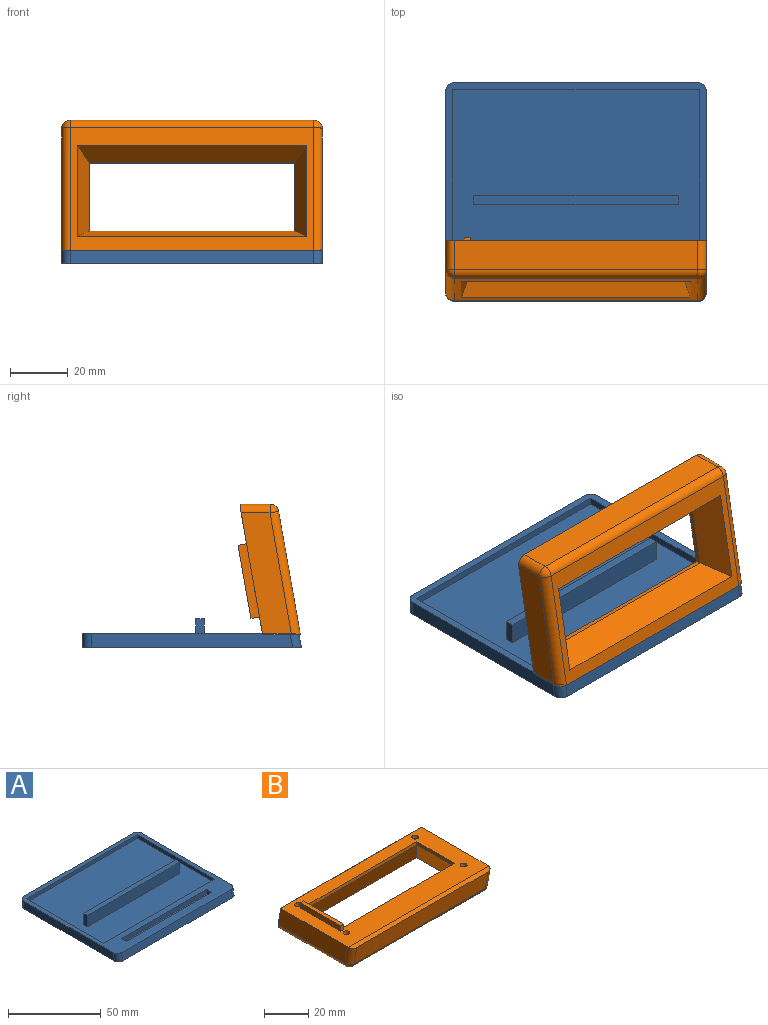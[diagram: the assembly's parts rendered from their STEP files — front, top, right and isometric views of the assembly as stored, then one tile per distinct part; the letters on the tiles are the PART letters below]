
ASSEMBLY  parts=2 mates=1
PART A: 25 faces, bbox 90x75.5x10.5 mm
  f0: plane 85x59.56mm, normal (0,0,1), area 4851mm2, adj f1,f2,f3,f4,f21,f22,f23,f24
  f1: plane 59.56x2.5mm, normal (-1,0,0), area 148.3mm2, adj f0,f2,f3,f9
  f2: plane 85x2.5mm, normal (0,-1,0), area 212.5mm2, adj f0,f1,f4,f9
  f3: plane 85x2.5mm, normal (0,0.98,-0.17), area 215.8mm2, adj f0,f1,f4,f9
  f4: plane 59.56x2.5mm, normal (1,0,0), area 148.3mm2, adj f0,f2,f3,f9
  f5: cylinder r=3mm len=5mm, axis (0,0,1), area 23.6mm2, adj f6,f8,f9,f11
  f6: plane 84x5mm, normal (0,1,0), area 420mm2, adj f5,f7,f8,f9
  f7: cylinder r=3mm len=5mm, axis (0,0,-1), area 23.6mm2, adj f6,f8,f9,f12
  f8: plane 90x75.5mm, normal (0,0,-1), area 6787.2mm2, adj f5,f6,f7,f10,f11,f12,f18,f19
  f9: plane 90x74.62mm, normal (0,0,1), area 1421.9mm2, adj f1,f2,f3,f4,f5,f6,f7,f10
  f10: plane 84x5mm, normal (0,-0.98,0.17), area 426.5mm2, adj f8,f9,f18,f19
  f11: plane 69.45x5mm, normal (-1,0,0), area 345.1mm2, adj f5,f8,f9,f18
  f12: plane 69.45x5mm, normal (1,0,0), area 345.1mm2, adj f7,f8,f9,f19
  f13: plane 65.22x3mm, normal (0,-1,0), area 195.7mm2, adj f9,f14,f16,f17
  f14: plane 4x3mm, normal (1,0,0), area 12mm2, adj f9,f13,f15,f17
  f15: plane 65.22x3mm, normal (0,1,0), area 195.7mm2, adj f9,f14,f16,f17
  f16: plane 4x3mm, normal (-1,0,0), area 12mm2, adj f9,f13,f15,f17
  f17: plane 65.22x4mm, normal (0,0,1), area 260.9mm2, adj f13,f14,f15,f16
  f18: cylinder r=3mm len=6.04mm, axis (0,0.17,0.98), area 23.9mm2, adj f8,f9,f10,f11
  f19: cylinder r=3mm len=6.04mm, axis (0,-0.17,-0.98), area 23.9mm2, adj f8,f9,f10,f12
  f20: plane 70.5x3mm, normal (0,0,1), area 211.5mm2, adj f21,f22,f23,f24
  f21: plane 7.5x3mm, normal (1,0,0), area 22.5mm2, adj f0,f20,f22,f24
  f22: plane 70.5x7.5mm, normal (0,-1,0), area 528.7mm2, adj f0,f20,f21,f23
  f23: plane 7.5x3mm, normal (-1,0,0), area 22.5mm2, adj f0,f20,f22,f24
  f24: plane 70.5x7.5mm, normal (0,1,0), area 528.7mm2, adj f0,f20,f21,f23
PART B: 40 faces, bbox 90x49.2x15.8 mm
  f0: plane 2.37x2.37mm, normal (0,0,1), area 4.4mm2, adj f12
  f1: plane 2.37x2.37mm, normal (0,0,1), area 4.4mm2, adj f13
  f2: plane 2.37x2.37mm, normal (0,0,1), area 4.4mm2, adj f14
  f3: plane 2.37x2.37mm, normal (0,0,1), area 4.4mm2, adj f15
  f4: plane 84x9.89mm, normal (0,-0.98,-0.17), area 843.5mm2, adj f5,f6,f7,f20
  f5: cylinder r=3mm len=10.41mm, axis (0,0.17,-0.98), area 47.3mm2, adj f4,f6,f21,f23,f28
  f6: plane 89.92x2.46mm, normal (0,-0.17,0.98), area 221.2mm2, adj f4,f5,f7,f23
  f7: cylinder r=3mm len=10.41mm, axis (0,-0.17,0.98), area 47.3mm2, adj f4,f6,f22,f23,f27
  f8: plane 24x1.8mm, normal (1,0,0), area 43.3mm2, adj f9,f11,f18,f23
  f9: plane 71x1.8mm, normal (0,1,0), area 128mm2, adj f8,f10,f17,f23
  f10: plane 24x1.8mm, normal (-1,0,0), area 43.3mm2, adj f9,f11,f16,f23
  f11: plane 71x1.8mm, normal (0,-1,0), area 128mm2, adj f8,f10,f19,f23
  f12: cone r=1.5mm half-angle=3deg, axis (0,0,1), area 50.7mm2, adj f0,f23
  f13: cone r=1.5mm half-angle=3deg, axis (0,0,1), area 50.7mm2, adj f1,f23
  f14: cone r=1.5mm half-angle=3deg, axis (0,0,1), area 50.7mm2, adj f2,f23
  f15: cone r=1.5mm half-angle=3deg, axis (0,0,1), area 50.7mm2, adj f3,f23
  f16: plane 32x11mm, normal (-0.94,0,-0.34), area 327.7mm2, adj f10,f17,f19,f26
  f17: plane 79x11mm, normal (0,0.94,-0.34), area 877.9mm2, adj f9,f16,f18,f26
  f18: plane 32x11mm, normal (0.94,0,-0.34), area 327.7mm2, adj f8,f17,f19,f26
  f19: plane 79x11mm, normal (0,-0.94,-0.34), area 877.9mm2, adj f11,f16,f18,f26
  f20: cylinder r=3mm len=84mm, axis (1,0,0), area 351.9mm2, adj f4,f21,f22,f26
  f21: sphere r=3mm, area 12.6mm2, adj f5,f20,f25
  f22: sphere r=3mm, area 12.6mm2, adj f7,f20,f24
  f23: plane 90x43.16mm, normal (0,0,1), area 2100.4mm2, adj f5,f6,f7,f8,f9,f10,f11,f12
  f24: cylinder r=3mm len=43.18mm, axis (0,-1,0), area 202.6mm2, adj f22,f26,f27,f29
  f25: cylinder r=3mm len=43.18mm, axis (0,1,0), area 202.6mm2, adj f21,f26,f28,f29
  f26: plane 84x43.18mm, normal (0,0,-1), area 1098.9mm2, adj f16,f17,f18,f19,f20,f24,f25,f29
  f27: plane 44.38x9.8mm, normal (-1,0,0), area 418.1mm2, adj f7,f23,f24,f29
  f28: plane 44.38x9.8mm, normal (1,0,0), area 418.1mm2, adj f5,f23,f25,f29
  f29: plane 90x12.8mm, normal (0,0.98,0.17), area 976.4mm2, adj f23,f24,f25,f26,f27,f28,f30,f31
  f30: plane 63.22x2.46mm, normal (0,-0.17,0.98), area 158.1mm2, adj f29,f31,f33,f34
  f31: plane 3.39x2.98mm, normal (1,0,0), area 7.5mm2, adj f29,f30,f32,f34
  f32: plane 63.22x2.46mm, normal (0,0.17,-0.98), area 158.1mm2, adj f29,f31,f33,f34
  f33: plane 3.39x2.98mm, normal (-1,0,0), area 7.5mm2, adj f29,f30,f32,f34
  f34: plane 63.22x2.95mm, normal (0,0.98,0.17), area 189.7mm2, adj f30,f31,f32,f33
  f35: plane 25.66x3mm, normal (-1,0,0), area 77mm2, adj f23,f36,f38,f39
  f36: plane 3x2mm, normal (0,-1,0), area 6mm2, adj f23,f35,f37,f39
  f37: plane 25.66x3mm, normal (1,0,0), area 77mm2, adj f23,f36,f38,f39
  f38: plane 3x2mm, normal (0,1,0), area 6mm2, adj f23,f35,f37,f39
  f39: plane 25.66x2mm, normal (0,0,1), area 51.3mm2, adj f35,f36,f37,f38
PLACE A t=(-15.98,35.09,36.12)mm
PLACE B rot(axis=(-1,0,0),100deg) t=(-15.98,-25.13,-30.42)mm
MATE fastened B.f34 <-> A.f17  axis (0,0,-1) through (-15.98,0.48,38.12)mm
